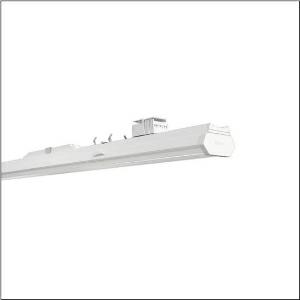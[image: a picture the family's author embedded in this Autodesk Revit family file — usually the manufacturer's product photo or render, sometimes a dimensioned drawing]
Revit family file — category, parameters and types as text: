
# Revit family: licross_r__21_protected_ho_52td12dn4e5m_4ef7
name_source: partatom
category: Lighting Fixtures
units: mm (PartAtom-declared; Revit-internal decimal feet)

## family parameters
Cut with Voids When Loaded = No
Host = Face
Light Source = No
Part Type = Normal
Room Calculation Point = No
Round Connector Dimension = Use Diameter
Shared = No

## types (1)
- --- (1 x LED, 14690 lm, 84.9 W, 4000K)
    Apparent Load = 85 VA
    CIE Flux Codes = 70 91 97 98 100
    Color Rendering = 80
    Color Temperature = 4000K
    Default Elevation = 1800 mm
    Description = Licross® 21 Protected HO, luminaire insert, of sheet steel, galvanised, coil coated, white, length: 1.500mm, width: 90mm, height: 103mm, LED rated luminous flux: 14.690lm, light colour: 840, control gear: DALI 2, with plug, 5-pole, with phase selection, mains connection: 220..240V, AC, 50/60Hz, rated input power: 85W, halogen-free wiring, primary light control with lens, of plastic, primary optical cover: cover, of PMMA, light emission: direct distribution, primary light characteristic: symmetric, protection rating (complete): IP54, insulation class (complete): insulation class I (protective earthing), certification: CE, ENEC, VDE, UKCA, protection symbol: D if used in an environment with non-conductive dust loads with corresponding accessories, impact resistance: IK06, permissible ambient temperature for indoor applications: -25..+35°C, corresponds to IFS (International Featured Standards) requirements for safety and quality in the food industry, reducing of maximum allowable ambient temperature of 5°C with ceiling mounting, LABS conformity tested according to VDMA 24364:2018-05, packaging unit: 1 piece
    Height = 92 mm
    Lamp = 1 x LED
    Lamp Light Flux = 14690 lm
    Lamp Power = 84.9 W
    Lamp count = 1
    Length = 1500 mm
    Luminous efficacy = 173 lm/W
    Manufacturer = Siteco
    ModVariant = No
    Model = 52TD12DN4E5M
    Mounting Place = Ceiling
    Mounting Type = Pendant
    Number of Poles = 1
    OnlyDefault = Yes
    Power Factor = 1
    Product Name = Licross® 21 Protected HO
    Product group = luminaire insert
    ProductGroupID = 902
    Protection Class = Protection class I
    Protection Degree = IP 54
    RLX_Detail_Level = 1
    RLX_Emergency_Light_Flux = 0 lm
    RLX_Emergency_Type = 0
    RLX_Emergency_Type_DB = No
    RlxData = <blob elided: 24345 chars, md5=11c84377>
    Socket = socket
    Standby Power = 0 W
    System Light Flux = 14690 lm
    System Power = 85 W
    Type Comments = factory setting: luminous flux: 100 % | dim-lin: 254 | 484 mA
    Type Image = l_1256148.jpg
    URL = http://relux.com
    VarID = @adj_129010
    Voltage = 0 V
    Weight = 0.00 kg
    Width = 88 mm

## geometry (parser evidence)
native form markers: Blend x4, Sweep x11
no freeform markers — native parametric forms only
